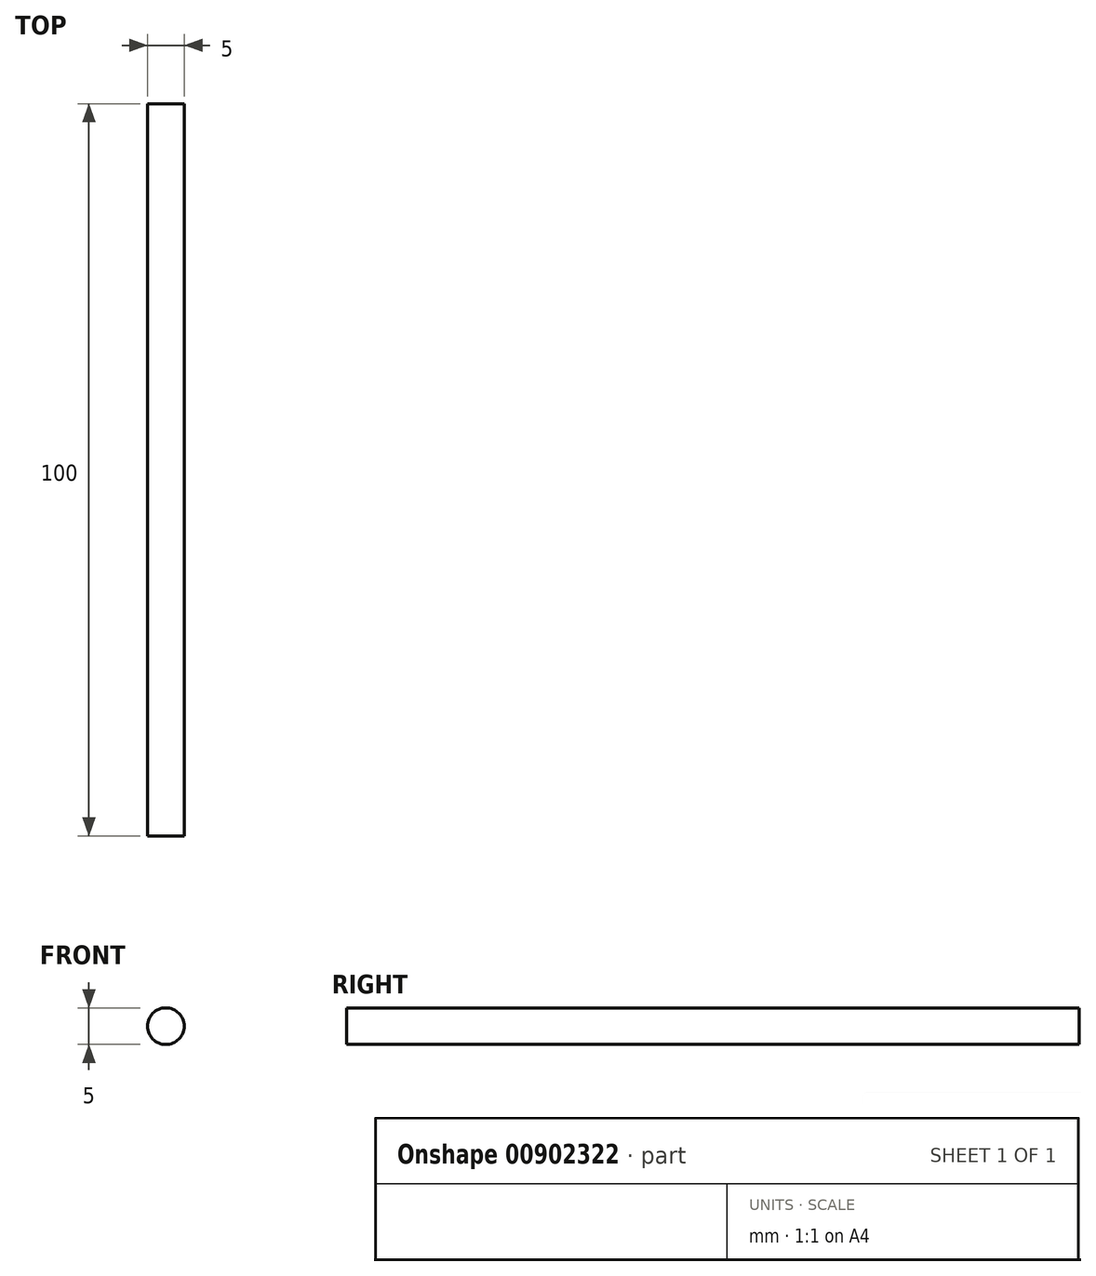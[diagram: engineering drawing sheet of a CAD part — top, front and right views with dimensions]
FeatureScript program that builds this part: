
annotation { "Feature Type Name" : "Feature", "Feature Type Description" : "" }
export const myFeature = defineFeature(function(context is Context, id is Id, definition is map)
    precondition{}
    {
        {
            var Q0;
            Q0=qCreatedBy(makeId("Front.planeOp"),FACE);
            var sketch = newSketch(context, id + "F0", { "sketchPlane" : qUnion([Q0])});
            skCircle(sketch, "E0", {"center": v(0, 0) * mm, "radius": 2.5 * mm});
            skSolve(sketch);
        }
        {
            var Q0;
            Q0 = qSketchRegion(id + "F0", true);
            extrude(context, id + "F1", {"entities" : qUnion([Q0]), "endBound" : BoundingType.SYMMETRIC, "depth" : 100 * mm, "offsetDistance" : 25 * mm});
        }
    });
